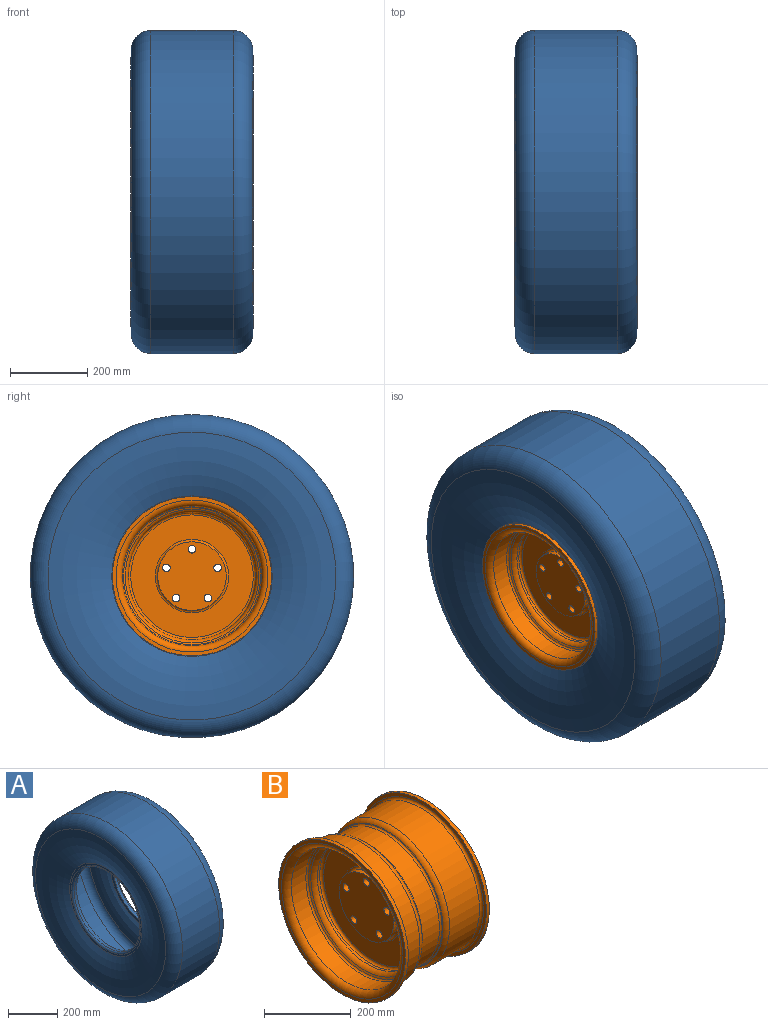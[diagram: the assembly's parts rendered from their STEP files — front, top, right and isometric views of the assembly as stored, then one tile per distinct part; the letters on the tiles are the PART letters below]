
ASSEMBLY  parts=2 mates=1
PART A: 18 faces, bbox 317.5x1211.9x1211.9 mm
  f0: cylinder r=419.1mm len=838.2mm, axis (-1,0,0), area 562089mm2, adj f1,f17
  f1: torus R=368.3mm, axis (-1,0,0), area 189256.5mm2, adj f0,f2
  f2: torus R=343.41mm, axis (-1,0,0), area 309402.4mm2, adj f1,f3
  f3: plane 415.93x415.93mm, normal (-1,0,0), area 12161mm2, adj f2,f4
  f4: torus R=198.44mm, axis (-1,0,0), area 15149.7mm2, adj f3,f5
  f5: cylinder r=190.5mm len=381mm, axis (-1,0,0), area 17101.4mm2, adj f4,f6
  f6: plane 413.04x413.04mm, normal (1,0,0), area 19980mm2, adj f5,f7
  f7: torus R=343.41mm, axis (-1,0,0), area 308307.1mm2, adj f6,f8
  f8: torus R=368.3mm, axis (-1,0,0), area 114503.3mm2, adj f7,f9
  f9: cylinder r=400.05mm len=800.1mm, axis (-1,0,0), area 536539.5mm2, adj f8,f10
  f10: torus R=368.3mm, axis (-1,0,0), area 114503.3mm2, adj f9,f11
  f11: torus R=343.41mm, axis (-1,0,0), area 308307.1mm2, adj f10,f12
  f12: plane 413.04x413.04mm, normal (-1,0,0), area 19980mm2, adj f11,f13
  f13: cylinder r=190.5mm len=381mm, axis (-1,0,0), area 17101.4mm2, adj f12,f14
  f14: torus R=198.44mm, axis (-1,0,0), area 15149.7mm2, adj f13,f15
  f15: plane 415.93x415.93mm, normal (1,0,0), area 12161mm2, adj f14,f16
  f16: torus R=343.41mm, axis (-1,0,0), area 309402.4mm2, adj f15,f17
  f17: torus R=368.3mm, axis (-1,0,0), area 189256.5mm2, adj f0,f16
PART B: 41 faces, bbox 273.1x450.5x450.5 mm
  f0: torus R=174.62mm, axis (-1,0,0), area 19611.5mm2, adj f1,f35
  f1: cylinder r=190.5mm len=381mm, axis (-1,0,0), area 56436.7mm2, adj f0,f2
  f2: torus R=196.85mm, axis (-1,0,0), area 12083.6mm2, adj f1,f3
  f3: plane 412.75x412.75mm, normal (1,0,0), area 12066mm2, adj f2,f4
  f4: cylinder r=206.38mm len=412.75mm, axis (-1,0,0), area 12351mm2, adj f3,f5
  f5: plane 412.75x412.75mm, normal (-1,0,0), area 12066mm2, adj f4,f6
  f6: torus R=196.85mm, axis (-1,0,0), area 29259mm2, adj f5,f7
  f7: cylinder r=180.97mm len=361.95mm, axis (-1,0,0), area 53614.8mm2, adj f6,f8
  f8: torus R=174.62mm, axis (-1,0,0), area 7515.5mm2, adj f7,f9
  f9: cone r=177.8mm half-angle=60deg, axis (-1,0,0), area 6061.2mm2, adj f8,f10
  f10: torus R=180.97mm, axis (-1,0,0), area 17532.1mm2, adj f9,f11
  f11: cylinder r=165.1mm len=330.2mm, axis (-1,0,0), area 7469.7mm2, adj f10,f12
  f12: torus R=158.75mm, axis (-1,0,0), area 10202.5mm2, adj f11,f13
  f13: plane 317.5x317.5mm, normal (-1,0,0), area 50670.7mm2, adj f12,f14
  f14: torus R=95.25mm, axis (-1,0,0), area 5716.2mm2, adj f13,f15
  f15: cylinder r=88.9mm len=177.8mm, axis (-1,0,0), area 7093.9mm2, adj f14,f16
  f16: plane 177.8x177.8mm, normal (-1,0,0), area 23287.3mm2, adj f15,f36,f37,f38,f39,f40
  f17: plane 317.5x317.5mm, normal (1,0,0), area 77631.6mm2, adj f18,f36,f37,f38,f39,f40
  f18: torus R=158.75mm, axis (-1,0,0), area 10202.5mm2, adj f17,f19
  f19: cylinder r=165.1mm len=330.2mm, axis (-1,0,0), area 7469.7mm2, adj f18,f20
  f20: torus R=180.97mm, axis (-1,0,0), area 17532.1mm2, adj f19,f21
  f21: cone r=173.04mm half-angle=60deg, axis (1,0,0), area 6061.2mm2, adj f20,f22
  f22: torus R=174.62mm, axis (-1,0,0), area 7515.5mm2, adj f21,f23
  f23: cylinder r=180.97mm len=361.95mm, axis (-1,0,0), area 111042.2mm2, adj f22,f24
  f24: torus R=196.85mm, axis (-1,0,0), area 29259mm2, adj f23,f25
  f25: plane 412.75x412.75mm, normal (1,0,0), area 12066mm2, adj f24,f26
  f26: cylinder r=206.38mm len=412.75mm, axis (-1,0,0), area 12351mm2, adj f25,f27
  f27: plane 412.75x412.75mm, normal (-1,0,0), area 12066mm2, adj f26,f28
  f28: torus R=196.85mm, axis (-1,0,0), area 12083.6mm2, adj f27,f29
  f29: cylinder r=190.5mm len=381mm, axis (-1,0,0), area 116886.5mm2, adj f28,f30
  f30: torus R=174.62mm, axis (-1,0,0), area 19611.5mm2, adj f29,f31
  f31: cone r=180.97mm half-angle=60deg, axis (1,0,0), area 2093.5mm2, adj f30,f32
  f32: torus R=184.15mm, axis (-1,0,0), area 7474.6mm2, adj f31,f33
  f33: cylinder r=177.8mm len=355.6mm, axis (-1,0,0), area 62747.7mm2, adj f32,f34
  f34: torus R=184.15mm, axis (-1,0,0), area 7474.6mm2, adj f33,f35
  f35: cone r=182.56mm half-angle=60deg, axis (-1,0,0), area 2093.5mm2, adj f0,f34
  f36: cylinder r=9.91mm len=44.45mm, axis (-1,0,0), area 2766.6mm2, adj f16,f17
  f37: cylinder r=9.91mm len=44.45mm, axis (-1,0,0), area 2766.6mm2, adj f16,f17
  f38: cylinder r=9.91mm len=44.45mm, axis (-1,0,0), area 2766.6mm2, adj f16,f17
  f39: cylinder r=9.91mm len=44.45mm, axis (-1,0,0), area 2766.6mm2, adj f16,f17
  f40: cylinder r=9.91mm len=44.45mm, axis (-1,0,0), area 2766.6mm2, adj f16,f17
PLACE A t=(-79.52,0,0)mm
PLACE B t=(-79.52,0,0)mm
MATE fastened A.f0 <-> B.f0  axis (-1,0,0) through (-70,0,0)mm
